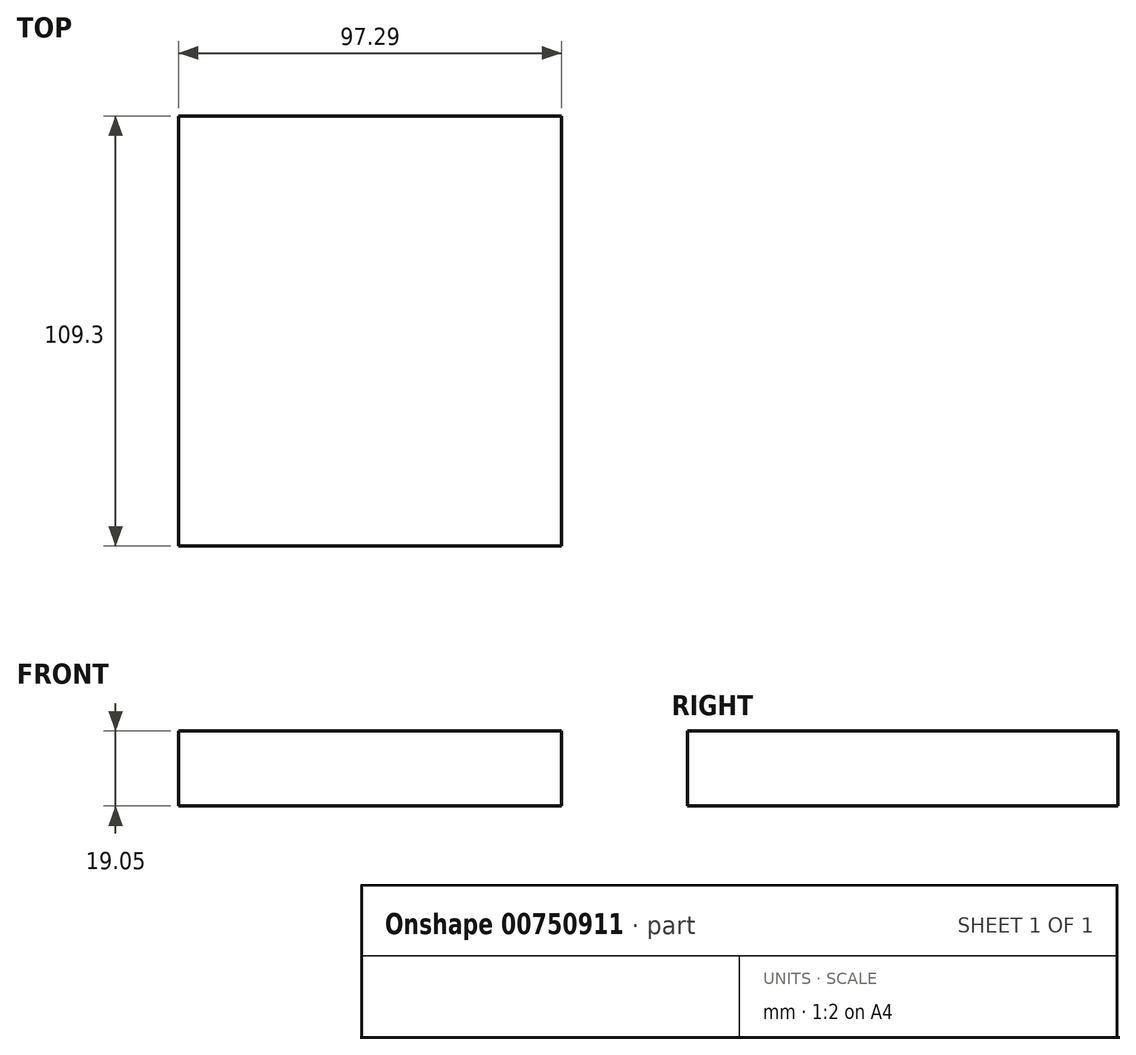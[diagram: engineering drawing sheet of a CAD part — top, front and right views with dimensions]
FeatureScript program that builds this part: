
annotation { "Feature Type Name" : "Feature", "Feature Type Description" : "" }
export const myFeature = defineFeature(function(context is Context, id is Id, definition is map)
    precondition{}
    {
        {
            var Q0;
            Q0=qCreatedBy(makeId("Top.planeOp"),FACE);
            var sketch = newSketch(context, id + "F0", { "sketchPlane" : qUnion([Q0])});
            skLineSegment(sketch, "E0.bottom", {"start": v(-48, 52.92) * mm, "end": v(49.29, 52.92) * mm});
            skLineSegment(sketch, "E0.top", {"start": v(-48, -56.38) * mm, "end": v(49.29, -56.38) * mm});
            skLineSegment(sketch, "E0.left", {"start": v(-48, 52.92) * mm, "end": v(-48, -56.38) * mm});
            skLineSegment(sketch, "E0.right", {"start": v(49.29, 52.92) * mm, "end": v(49.29, -56.38) * mm});
            skSolve(sketch);
        }
        {
            var Q0;
            Q0 = qSketchRegion(id + "F0", true);
            extrude(context, id + "F1", {"entities" : qUnion([Q0]), "depth" : 19.05 * mm, "offsetDistance" : 25.4 * mm});
        }
    });
